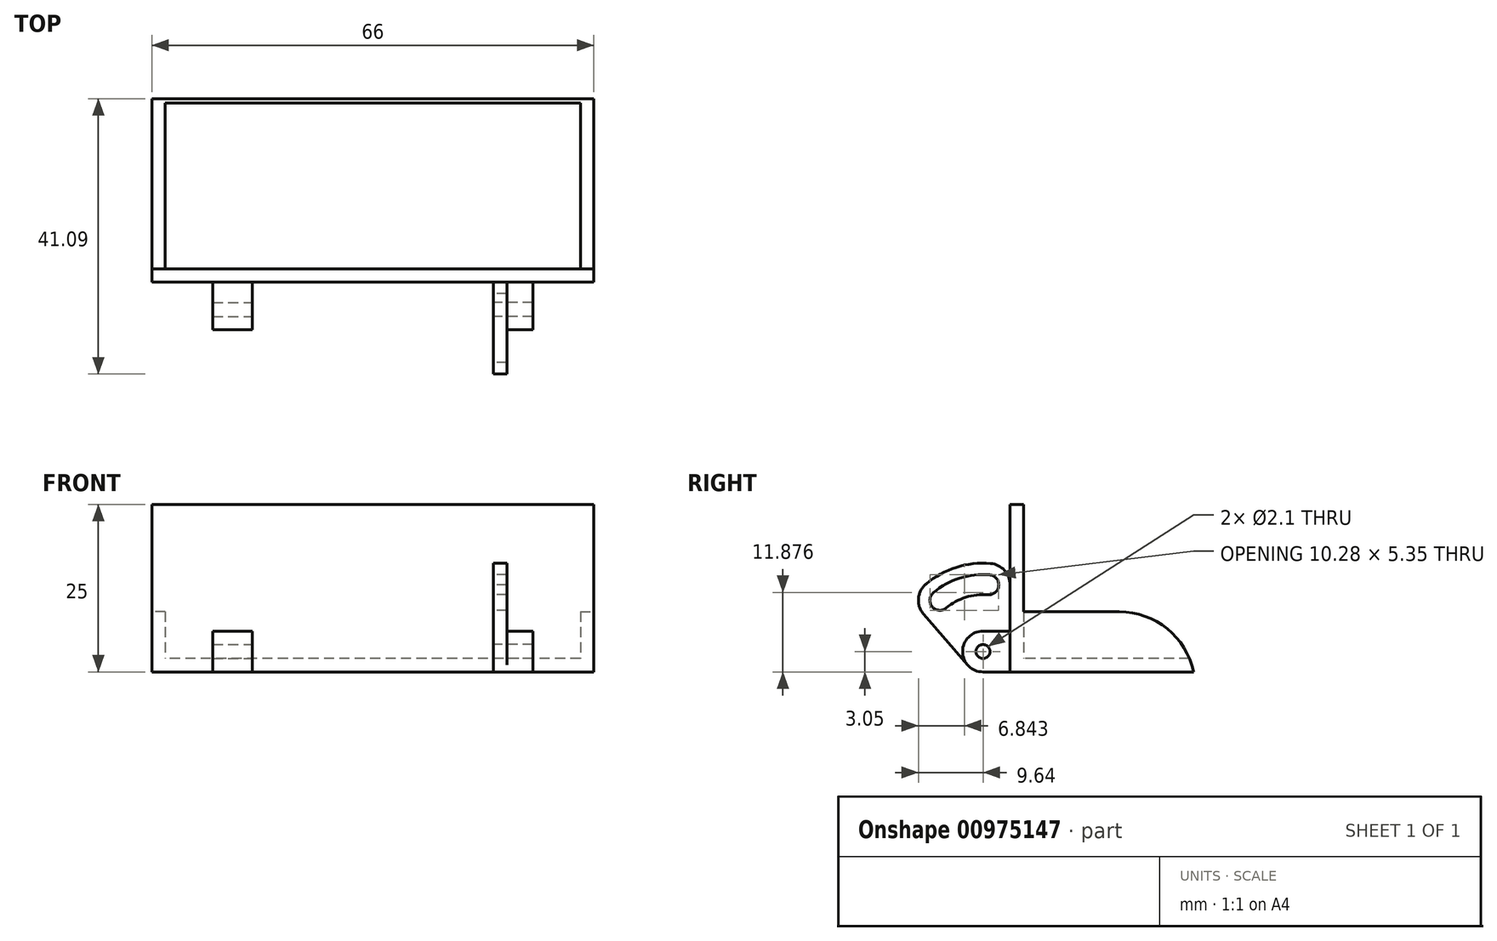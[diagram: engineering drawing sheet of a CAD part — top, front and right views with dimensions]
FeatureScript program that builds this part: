
annotation { "Feature Type Name" : "Feature", "Feature Type Description" : "" }
export const myFeature = defineFeature(function(context is Context, id is Id, definition is map)
    precondition{}
    {
        {
            var Q0;
            Q0=qCreatedBy(makeId("Top.planeOp"),FACE);
            var sketch = newSketch(context, id + "F0", { "sketchPlane" : qUnion([Q0])});
            skLineSegment(sketch, "E0.bottom", {"start": v(-31, -12.7) * mm, "end": v(31, -12.7) * mm});
            skLineSegment(sketch, "E0.top", {"start": v(-31, 12.7) * mm, "end": v(31, 12.7) * mm});
            skLineSegment(sketch, "E0.left", {"start": v(-31, -12.7) * mm, "end": v(-31, 12.7) * mm});
            skLineSegment(sketch, "E0.right", {"start": v(31, -12.7) * mm, "end": v(31, 12.7) * mm});
            skPoint(sketch, "E0.middle", {"position": v(0, 0) * mm});
            skLineSegment(sketch, "E1.0", {"start": v(-33, 14.7) * mm, "end": v(33, 14.7) * mm, "construction": true});
            skLineSegment(sketch, "E1.1", {"start": v(-33, -14.7) * mm, "end": v(-33, 14.7) * mm});
            skLineSegment(sketch, "E1.2", {"start": v(-33, -14.7) * mm, "end": v(33, -14.7) * mm});
            skLineSegment(sketch, "E1.3", {"start": v(33, -14.7) * mm, "end": v(33, 14.7) * mm});
            skLineSegment(sketch, "E2", {"start": v(-31, -12.7) * mm, "end": v(-33, -12.7) * mm});
            skLineSegment(sketch, "E3", {"start": v(31, -12.7) * mm, "end": v(33, -12.7) * mm});
            skLineSegment(sketch, "E4", {"start": v(-31, 12.7) * mm, "end": v(-33, 12.7) * mm});
            skLineSegment(sketch, "E5", {"start": v(31, 12.7) * mm, "end": v(33, 12.7) * mm});
            skSolve(sketch);
        }
        {
            var Q0;
            Q0 = qSketchRegion(id + "F0", true);
            var Q1;
            Q1=makeQuery(id+"F0.imprint","IMPRINT",FACE,{"disambiguationData":[TD([[makeQuery(id+"F0.imprint","IMPRINT",EDGE,{"derivedFrom":sQuery(id+"F0.wireOp",EDGE,"E0.bottom")}),1.0]])]});
            var Q2;
            {var subQ0=sQuery(id+"F0.wireOp",EDGE,"E0.top");Q2=makeQuery(id+"F0.imprint","IMPRINT",FACE,{"disambiguationData":[TD([[makeQuery(id+"F0.imprint","IMPRINT",EDGE,{"derivedFrom":subQ0}),-1.0]])]});}
            extrude(context, id + "F1", {"entities" : qUnion([Q0, Q1, Q2]), "depth" : 2 * mm, "offsetDistance" : 25 * mm});
        }
        {
            var Q0;
            Q0=makeQuery(id+"F0.imprint","IMPRINT",FACE,{"disambiguationData":[TD([[makeQuery(id+"F0.imprint","IMPRINT",EDGE,{"derivedFrom":sQuery(id+"F0.wireOp",EDGE,"E0.bottom")}),-1.0]])]});
            extrude(context, id + "F2", {"entities" : qUnion([Q0]), "operationType" : NewBodyOperationType.ADD, "depth" : 25 * mm, "offsetDistance" : 25 * mm});
        }
        {
            var Q0;
            Q0=makeQuery(id+"F0.imprint","IMPRINT",FACE,{"disambiguationData":[TD([[makeQuery(id+"F0.imprint","IMPRINT",EDGE,{"derivedFrom":sQuery(id+"F0.wireOp",EDGE,"E0.left")}),1.0]])]});
            var Q1;
            Q1=makeQuery(id+"F0.imprint","IMPRINT",FACE,{"disambiguationData":[TD([[makeQuery(id+"F0.imprint","IMPRINT",EDGE,{"derivedFrom":sQuery(id+"F0.wireOp",EDGE,"E0.right")}),-1.0]])]});
            extrude(context, id + "F3", {"entities" : qUnion([Q0, Q1]), "operationType" : NewBodyOperationType.ADD, "depth" : 9 * mm, "offsetDistance" : 25 * mm});
        }
        {
            var Q0;
            Q0=qCreatedBy(makeId("Right.planeOp"),FACE);
            var sketch = newSketch(context, id + "F4", { "sketchPlane" : qUnion([Q0])});
            skArc(sketch, "E6", {"start": v(-18.75, 6.1) * mm, "mid": v(-21.8, 3.05) * mm, "end": v(-18.75, 0) * mm});
            skCircle(sketch, "E7", {"center": v(-18.75, 3.05) * mm, "radius": 1.05 * mm});
            skLineSegment(sketch, "E8", {"start": v(-18.75, 6.1) * mm, "end": v(-14.7, 6.1) * mm});
            skLineSegment(sketch, "E9.right", {"start": v(-14.7, 6.1) * mm, "end": v(-14.7, 0) * mm});
            skLineSegment(sketch, "E10", {"start": v(-18.75, 0) * mm, "end": v(-14.7, 0) * mm});
            skSolve(sketch);
        }
        {
            var Q0;
            Q0 = qSketchRegion(id + "F4", true);
            extrude(context, id + "F5", {"entities" : qUnion([Q0]), "depth" : (5.9 + 6 * 3) * mm, "offsetDistance" : 25 * mm, "hasSecondDirection" : true, "secondDirectionOppositeDirection" : true, "secondDirectionDepth" : -(6 * 3) * mm});
        }
        {
            var Q0;
            Q0=makeQuery(id+"F5.opExtrude","SWEPT_BODY",BODY,{"disambiguationData":[OSD([sQuery(id+"F4.wireOp",EDGE,"E6"),sQuery(id+"F4.wireOp",EDGE,"E7"),sQuery(id+"F4.wireOp",EDGE,"E8"),sQuery(id+"F4.wireOp",EDGE,"Y19KJi4Q-xX3U-1lw8-dTvb-lTLsloNXFbLN"),sQuery(id+"F4.wireOp",EDGE,"qm7PHdQL-4fNi-jIDa-4D8y-KKKB80PP2ExG"),sQuery(id+"F4.wireOp",EDGE,"6535184e-9c90-422a-ba1d-02569a86d6f0.0")])]});
            var Q1;
            Q1=qCreatedBy(makeId("Right.planeOp"),FACE);
            mirror(context, id + "F6", {"operationType" : NewBodyOperationType.ADD, "entities" : qUnion([Q0]), "mirrorPlane" : qUnion([Q1])});
        }
        {
            var Q0;
            Q0=makeQuery(id+"F3.opExtrude","CAP_EDGE",EDGE,{"disambiguationData":[OSD([sQuery(id+"F0.wireOp",EDGE,"E2")])],"isStart":false});
            var Q1;
            Q1=makeQuery(id+"F3.opExtrude","CAP_EDGE",EDGE,{"disambiguationData":[OSD([sQuery(id+"F0.wireOp",EDGE,"E3")])],"isStart":false});
            var Q2;
            Q2=makeQuery(id+"F3.opExtrude","CAP_EDGE",EDGE,{"disambiguationData":[OSD([sQuery(id+"F0.wireOp",EDGE,"E4")])],"isStart":false});
            fillet(context, id + "F7", {"entities" : qUnion([Q0, Q1, Q2]), "radius" : 11.35 * mm, "tangentPropagation" : true, "allowEdgeOverflow" : false});
        }
        {
            var Q0;
            Q0=makeQuery(id+"F5.opExtrude","CAP_FACE",FACE,{"disambiguationData":[OSD([sQuery(id+"F4.wireOp",EDGE,"E6"),sQuery(id+"F4.wireOp",EDGE,"E7"),sQuery(id+"F4.wireOp",EDGE,"E8"),sQuery(id+"F4.wireOp",EDGE,"E9.right"),sQuery(id+"F4.wireOp",EDGE,"E10")])],"isStart":true});
            var sketch = newSketch(context, id + "F8", { "sketchPlane" : qUnion([Q0])});
            skArc(sketch, "E11", {"start": v(17.63, 16.2) * mm, "mid": v(15.54, 15.18) * mm, "end": v(14.7, 13.01) * mm});
            skArc(sketch, "E12", {"start": v(27.61, 8.6) * mm, "mid": v(28.38, 10.94) * mm, "end": v(27.26, 13.14) * mm});
            skPoint(sketch, "E13.first.point", {"position": v(13.68, -5.57) * mm});
            skArc(sketch, "E14", {"start": v(27.26, 13.14) * mm, "mid": v(22.75, 15.63) * mm, "end": v(17.63, 16.2) * mm});
            skArc(sketch, "E15", {"start": v(17.77, 14.5) * mm, "mid": v(16.4, 12.89) * mm, "end": v(18.03, 11.52) * mm});
            skArc(sketch, "E16", {"start": v(24.23, 9.55) * mm, "mid": v(26.34, 9.73) * mm, "end": v(26.16, 11.84) * mm});
            skLineSegment(sketch, "E17", {"start": v(17.9, 13.01) * mm, "end": v(18.66, 4.1) * mm, "construction": true});
            skLineSegment(sketch, "E18", {"start": v(24.23, 9.55) * mm, "end": v(19.43, 3.85) * mm, "construction": true});
            skCircle(sketch, "E19.0", {"center": v(18.75, 3.05) * mm, "radius": 1.05 * mm});
            skLineSegment(sketch, "E20.0", {"start": v(14.7, 25) * mm, "end": v(14.7, 0) * mm});
            skLineSegment(sketch, "E21", {"start": v(27.61, 8.6) * mm, "end": v(21.05, 1.05) * mm});
            skArc(sketch, "E22", {"start": v(26.16, 11.84) * mm, "mid": v(22.23, 14.01) * mm, "end": v(17.77, 14.5) * mm});
            skArc(sketch, "E23", {"start": v(24.23, 9.55) * mm, "mid": v(21.32, 11.15) * mm, "end": v(18.03, 11.52) * mm});
            skArc(sketch, "E24.0", {"start": v(18.75, 6.1) * mm, "mid": v(21.8, 3.05) * mm, "end": v(18.75, 0) * mm});
            skLineSegment(sketch, "E25.0", {"start": v(18.75, 6.1) * mm, "end": v(14.7, 6.1) * mm});
            skSolve(sketch);
        }
        {
            var Q0;
            {var subQ0=sQuery(id+"F8.wireOp",EDGE,"E25.0");Q0=makeQuery(id+"F8.imprint","IMPRINT",FACE,{"disambiguationData":[TD([[makeQuery(id+"F8.imprint","IMPRINT",EDGE,{"derivedFrom":subQ0}),1.0]])]});}
            var Q1;
            {var subQ4=sQuery(id+"F8.wireOp",EDGE,"E11");Q1=makeQuery(id+"F8.imprint","IMPRINT",FACE,{"disambiguationData":[TD([[makeQuery(id+"F8.imprint","IMPRINT",EDGE,{"derivedFrom":subQ4}),1.0]])]});}
            extrude(context, id + "F9", {"entities" : qUnion([Q0, Q1]), "operationType" : NewBodyOperationType.ADD, "depth" : -2 * mm, "offsetDistance" : 25 * mm});
        }
    });
